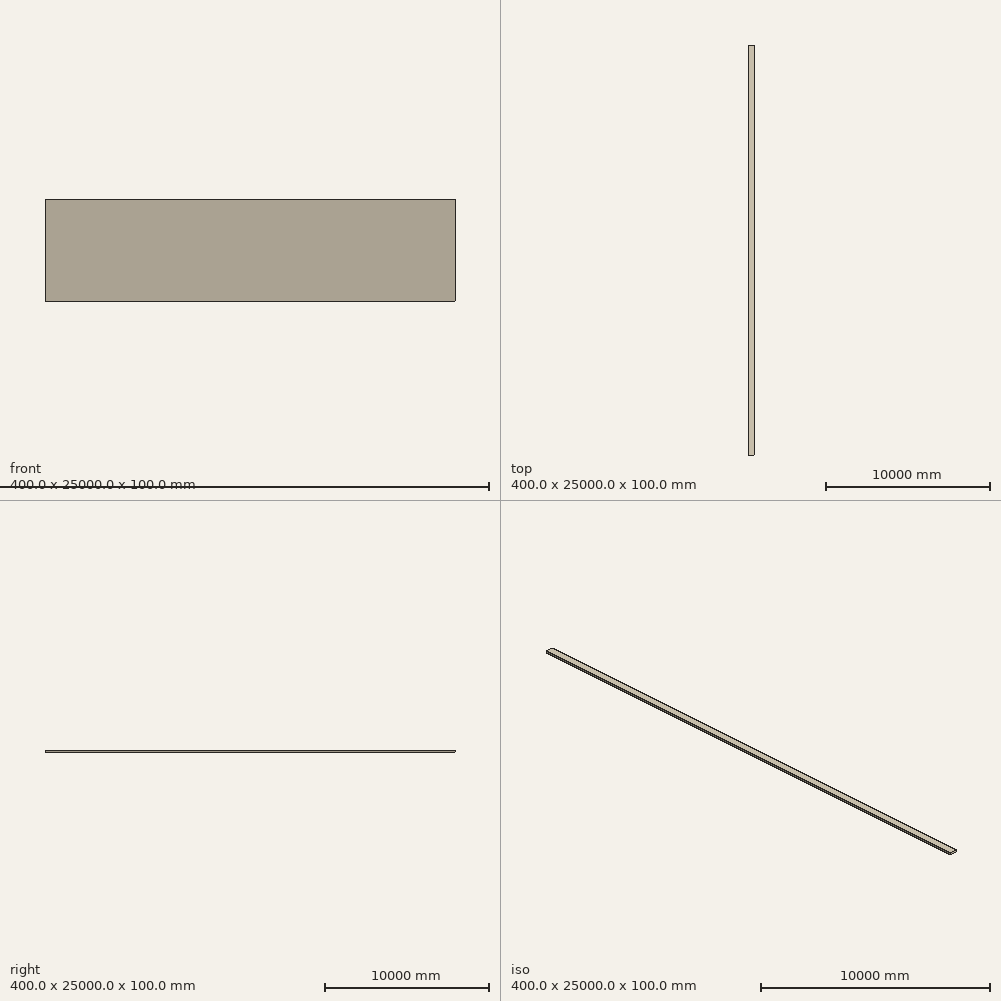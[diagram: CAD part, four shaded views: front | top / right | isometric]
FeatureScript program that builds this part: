
annotation { "Feature Type Name" : "Feature", "Feature Type Description" : "" }
export const myFeature = defineFeature(function(context is Context, id is Id, definition is map)
    precondition{}
    {
        {
            var Q0;
            Q0=qCreatedBy(makeId("Front.planeOp"),FACE);
            var sketch = newSketch(context, id + "F0", { "sketchPlane" : qUnion([Q0])});
            skLineSegment(sketch, "E0.bottom", {"start": v(0, 0) * mm, "end": v(400, 0) * mm});
            skLineSegment(sketch, "E0.top", {"start": v(0, 100) * mm, "end": v(400, 100) * mm});
            skLineSegment(sketch, "E0.left", {"start": v(0, 0) * mm, "end": v(0, 100) * mm});
            skLineSegment(sketch, "E0.right", {"start": v(400, 0) * mm, "end": v(400, 100) * mm});
            skSolve(sketch);
        }
        {
            var Q0;
            Q0 = qSketchRegion(id + "F0", true);
            extrude(context, id + "F1", {"entities" : qUnion([Q0]), "depth" : 25000 * mm, "offsetDistance" : 25 * mm});
        }
    });
